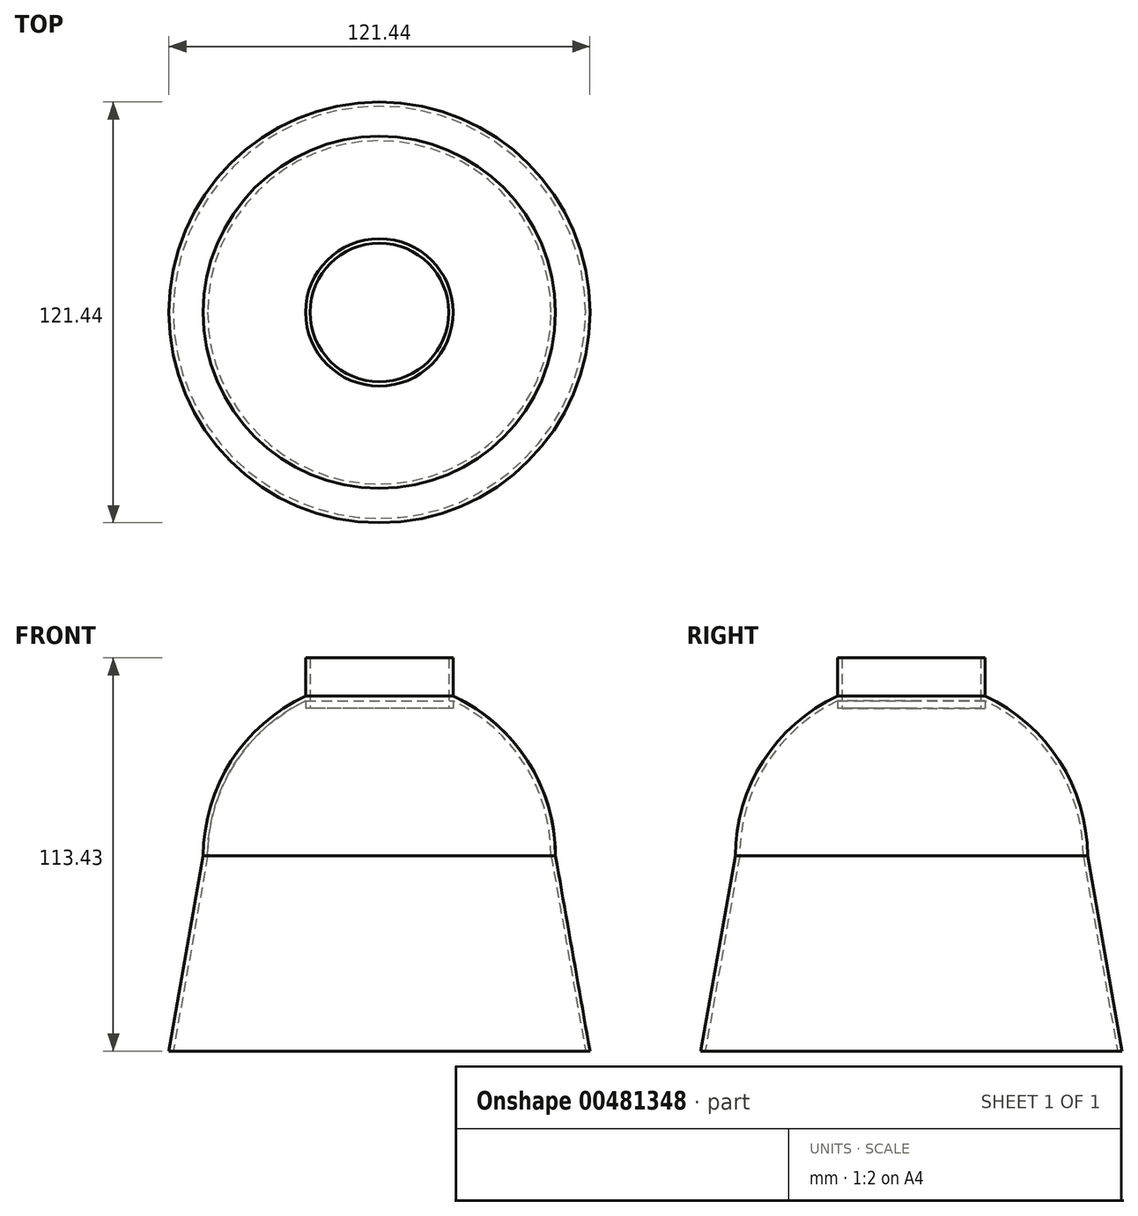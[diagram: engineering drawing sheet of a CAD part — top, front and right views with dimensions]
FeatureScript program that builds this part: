
annotation { "Feature Type Name" : "Feature", "Feature Type Description" : "" }
export const myFeature = defineFeature(function(context is Context, id is Id, definition is map)
    precondition{}
    {
        {
            var Q0;
            Q0=qCreatedBy(makeId("Front.planeOp"),FACE);
            var sketch = newSketch(context, id + "F0", { "sketchPlane" : qUnion([Q0])});
            skArc(sketch, "E0", {"start": v(0, 50.8) * mm, "mid": v(-35.92, 35.92) * mm, "end": v(-50.8, 0) * mm});
            skArc(sketch, "E1", {"start": v(0, 49.53) * mm, "mid": v(-35.02, 35.02) * mm, "end": v(-49.53, 0) * mm});
            skLineSegment(sketch, "E2.bottom", {"start": v(-49.53, 0) * mm, "end": v(-50.8, 0) * mm});
            skPoint(sketch, "E3.bottom.start.orphan", {"position": v(49.53, 0) * mm});
            skLineSegment(sketch, "E4", {"start": v(0, 50.8) * mm, "end": v(0, 49.53) * mm});
            skLineSegment(sketch, "E5", {"start": v(-49.53, 0) * mm, "end": v(-59.45, -56.28) * mm});
            skLineSegment(sketch, "E6", {"start": v(-50.8, 0) * mm, "end": v(-60.72, -56.28) * mm});
            skLineSegment(sketch, "E7", {"start": v(-59.45, -56.28) * mm, "end": v(-60.72, -56.28) * mm});
            skLineSegment(sketch, "E8", {"start": v(0, 50.8) * mm, "end": v(0, -56.28) * mm, "construction": true});
            skPoint(sketch, "E8.endSnap0", {"position": v(0, 50.17) * mm});
            skLineSegment(sketch, "E9", {"start": v(-60.72, -56.28) * mm, "end": v(0, -56.28) * mm, "construction": true});
            skLineSegment(sketch, "E10", {"start": v(-49.53, 0) * mm, "end": v(-49.53, -56.28) * mm, "construction": true});
            skSolve(sketch);
        }
        {
            var Q0;
            Q0=makeQuery(id+"F0.imprint","IMPRINT",FACE,{"disambiguationData":[TD([[makeQuery(id+"F0.imprint","IMPRINT",EDGE,{"derivedFrom":sQuery(id+"F0.wireOp",EDGE,"E0")}),1.0]])]});
            var Q1;
            Q1=makeQuery(id+"F0.imprint","IMPRINT",FACE,{"disambiguationData":[TD([[makeQuery(id+"F0.imprint","IMPRINT",EDGE,{"derivedFrom":sQuery(id+"F0.wireOp",EDGE,"E2.bottom")}),1.0]])]});
            var Q2;
            Q2=sQuery(id+"F0.wireOp",EDGE,"E8");
            revolve(context, id + "F1", {"entities" : qUnion([Q0, Q1]), "axis" : qUnion([Q2]), "revolveType" : RevolveType.FULL});
        }
        {
            var Q0;
            Q0=qCreatedBy(makeId("Top.planeOp"),FACE);
            var sketch = newSketch(context, id + "F2", { "sketchPlane" : qUnion([Q0])});
            skCircle(sketch, "E11", {"center": v(0, 0) * mm, "radius": 20 * mm});
            skCircle(sketch, "E12", {"center": v(0, 0) * mm, "radius": 21.27 * mm});
            skSolve(sketch);
        }
        {
            var Q0;
            Q0=qSketchRegion(id+"F2",true);
            extrude(context, id + "F3", {"entities" : qUnion([Q0]), "operationType" : NewBodyOperationType.ADD, "depth" : 57.15 * mm});
        }
        {
            var Q0;
            Q0=makeQuery(id+"F2.imprint","IMPRINT",FACE,{"disambiguationData":[TD([[makeQuery(id+"F2.imprint","IMPRINT",EDGE,{"derivedFrom":sQuery(id+"F2.wireOp",EDGE,"E11")}),1.0]])]});
            extrude(context, id + "F4", {"entities" : qUnion([Q0]), "operationType" : NewBodyOperationType.REMOVE, "endBound" : BoundingType.THROUGH_ALL, "depth" : 82.55 * mm});
        }
        {
            var Q0;
            Q0=makeQuery(id+"F2.imprint","IMPRINT",FACE,{"disambiguationData":[TD([[makeQuery(id+"F2.imprint","IMPRINT",EDGE,{"derivedFrom":sQuery(id+"F2.wireOp",EDGE,"E11")}),1.0]])]});
            var Q1;
            Q1=makeQuery(id+"F2.imprint","IMPRINT",FACE,{"disambiguationData":[TD([[makeQuery(id+"F2.imprint","IMPRINT",EDGE,{"derivedFrom":sQuery(id+"F2.wireOp",EDGE,"E11")}),-1.0]])]});
            extrude(context, id + "F5", {"entities" : qUnion([Q0, Q1]), "operationType" : NewBodyOperationType.REMOVE, "depth" : 42.55 * mm});
        }
    });
